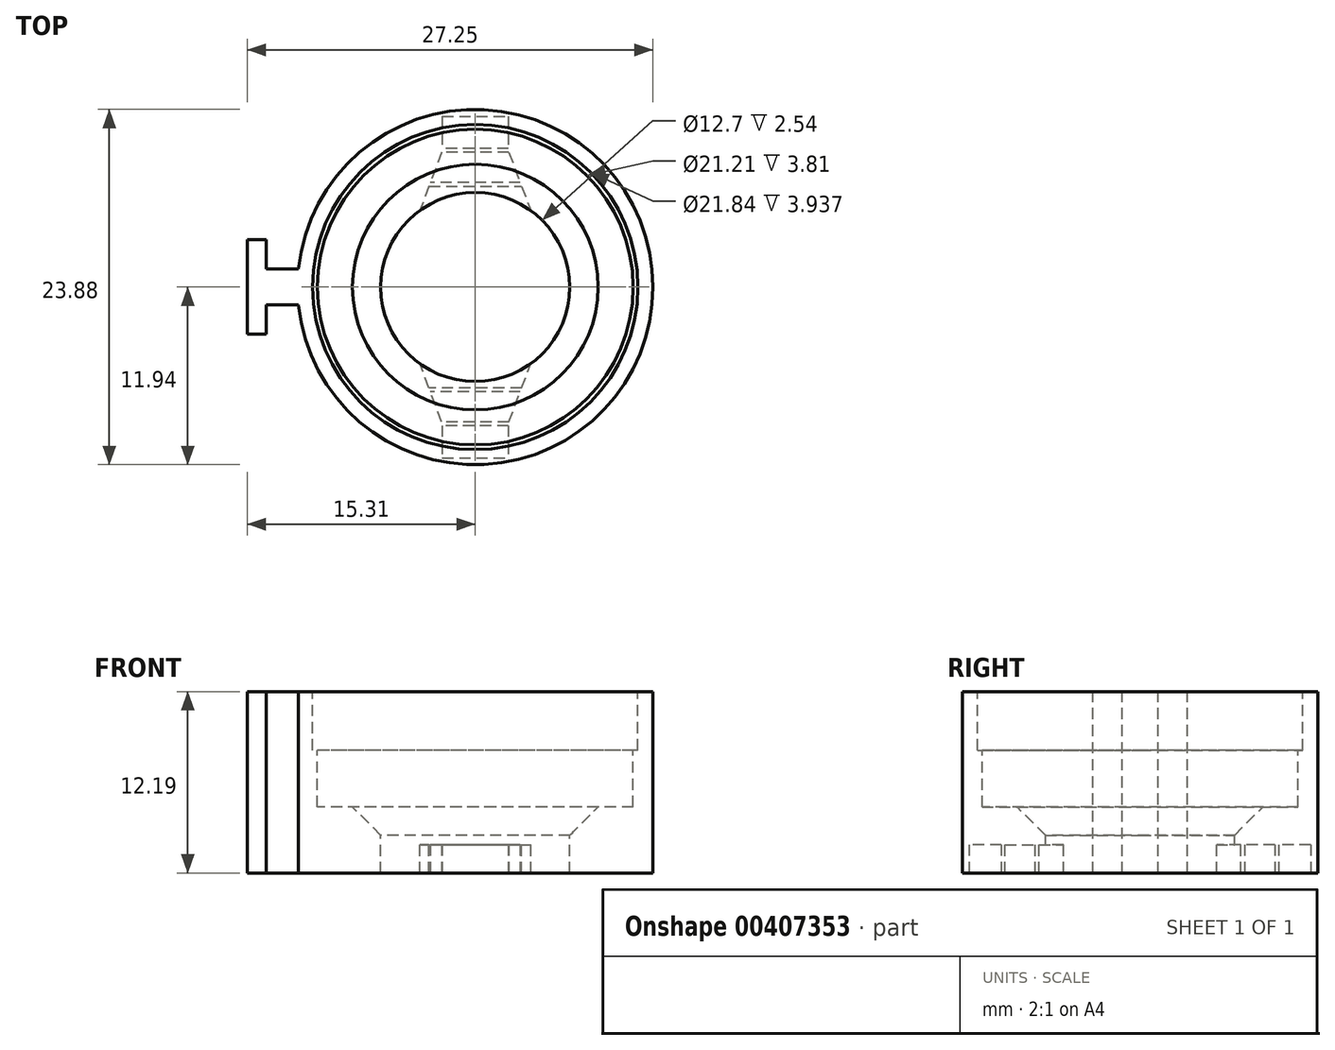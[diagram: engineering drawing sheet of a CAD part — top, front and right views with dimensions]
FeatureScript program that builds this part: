
annotation { "Feature Type Name" : "Feature", "Feature Type Description" : "" }
export const myFeature = defineFeature(function(context is Context, id is Id, definition is map)
    precondition{}
    {
        {
            var Q0;
            Q0=qCreatedBy(makeId("Top.planeOp"),FACE);
            var sketch = newSketch(context, id + "F0", { "sketchPlane" : qUnion([Q0])});
            skCircle(sketch, "E0", {"center": v(0, 0) * mm, "radius": 11.94 * mm});
            skSolve(sketch);
        }
        {
            var Q0;
            Q0 = qSketchRegion(id + "F0", true);
            extrude(context, id + "F1", {"entities" : qUnion([Q0]), "oppositeDirection" : true, "depth" : 12.2 * mm});
        }
        {
            var Q0;
            Q0=makeQuery(id+"F1.opExtrude","CAP_FACE",FACE,{"disambiguationData":[OSD([sQuery(id+"F0.wireOp",EDGE,"E0")])],"isStart":true});
            var sketch = newSketch(context, id + "F2", { "sketchPlane" : qUnion([Q0])});
            skCircle(sketch, "E1", {"center": v(0, 0) * mm, "radius": 6.35 * mm});
            skSolve(sketch);
        }
        {
            var Q0;
            Q0 = qSketchRegion(id + "F2", true);
            extrude(context, id + "F3", {"entities" : qUnion([Q0]), "operationType" : NewBodyOperationType.REMOVE, "endBound" : BoundingType.THROUGH_ALL, "oppositeDirection" : true, "depth" : 25.4 * mm});
        }
        {
            var Q0;
            Q0=makeQuery(id+"F1.opExtrude","CAP_FACE",FACE,{"disambiguationData":[OSD([sQuery(id+"F0.wireOp",EDGE,"E0")])],"isStart":true});
            var sketch = newSketch(context, id + "F4", { "sketchPlane" : qUnion([Q0])});
            skCircle(sketch, "E2", {"center": v(0, 0) * mm, "radius": 10.6 * mm});
            skSolve(sketch);
        }
        {
            var Q0;
            Q0 = qSketchRegion(id + "F4", true);
            extrude(context, id + "F5", {"entities" : qUnion([Q0]), "operationType" : NewBodyOperationType.REMOVE, "oppositeDirection" : true, "depth" : 7.75 * mm});
        }
        {
            var Q0;
            Q0=makeQuery(id+"F5.boolean.opBoolean","INTERSECT",EDGE,{"derivedFrom":[makeQuery(id+"F3.boolean.opBoolean","COPY",FACE,{"derivedFrom":makeQuery(id+"F3.opExtrude","SWEPT_FACE",FACE,{"disambiguationData":[OSD([sQuery(id+"F2.wireOp",EDGE,"E1")])]})}),makeQuery(id+"F5.opExtrude","CAP_FACE",FACE,{"disambiguationData":[OSD([sQuery(id+"F4.wireOp",EDGE,"E2")])],"isStart":false})]});
            chamfer(context, id + "F6", {"entities" : qUnion([Q0]), "width" : 1.9 * mm, "tangentPropagation" : true});
        }
        {
            var Q0;
            Q0=qCreatedBy(makeId("Top.planeOp"),FACE);
            var sketch = newSketch(context, id + "F7", { "sketchPlane" : qUnion([Q0])});
            skCircle(sketch, "E3", {"center": v(0, 0) * mm, "radius": 10.92 * mm});
            skSolve(sketch);
        }
        {
            var Q0;
            Q0 = qSketchRegion(id + "F7", true);
            extrude(context, id + "F8", {"entities" : qUnion([Q0]), "operationType" : NewBodyOperationType.REMOVE, "oppositeDirection" : true, "depth" : 3.94 * mm});
        }
        {
            var Q0;
            Q0=makeQuery(id+"F1.opExtrude","CAP_FACE",FACE,{"disambiguationData":[OSD([sQuery(id+"F0.wireOp",EDGE,"E0")])],"isStart":false});
            var sketch = newSketch(context, id + "F9", { "sketchPlane" : qUnion([Q0])});
            skLineSegment(sketch, "E4.bottom", {"start": v(2.22, -11.94) * mm, "end": v(-2.22, -11.94) * mm});
            skLineSegment(sketch, "E4.top", {"start": v(2.22, 11.94) * mm, "end": v(-2.22, 11.94) * mm});
            skLineSegment(sketch, "E4.left", {"start": v(2.22, -11.94) * mm, "end": v(2.22, 11.94) * mm});
            skLineSegment(sketch, "E4.right", {"start": v(-2.22, -11.94) * mm, "end": v(-2.22, 11.94) * mm});
            skPoint(sketch, "E4.middle", {"position": v(0, 0) * mm});
            skSolve(sketch);
        }
        {
            var Q0;
            Q0 = qSketchRegion(id + "F9", true);
            extrude(context, id + "F10", {"entities" : qUnion([Q0]), "operationType" : NewBodyOperationType.REMOVE, "oppositeDirection" : true, "depth" : 1.9 * mm});
        }
        {
            var Q0;
            {var subQ0=sQuery(id+"F0.wireOp",EDGE,"E0");Q0=makeQuery(id+"F10.boolean.opBoolean","SPLIT",FACE,{"disambiguationData":[TD([makeQuery(id+"F10.opExtrude","SWEPT_FACE",FACE,{"disambiguationData":[OSD([sQuery(id+"F9.wireOp",EDGE,"E4.right")])]})])],"derivedFrom":makeQuery(id+"F1.opExtrude","CAP_FACE",FACE,{"disambiguationData":[OSD([subQ0])],"isStart":false})});}
            cPlane(context, id + "F11", {"entities" : qUnion([Q0]), "cplaneType" : CPlaneType.OFFSET, "offset" : 0 * mm, "width" : 152.4 * mm, "height" : 152.4 * mm});
        }
        {
            var Q0;
            Q0=qCreatedBy(id+"F11.planeOp",FACE);
            var sketch = newSketch(context, id + "F12", { "sketchPlane" : qUnion([Q0])});
            skLineSegment(sketch, "E5", {"start": v(-27.4, 0) * mm, "end": v(27.4, 0) * mm, "construction": true});
            skLineSegment(sketch, "E6", {"start": v(0, 19.3) * mm, "end": v(0, -27.43) * mm, "construction": true});
            skLineSegment(sketch, "E7", {"start": v(-2.22, 9.14) * mm, "end": v(-5.08, 1.52) * mm});
            skLineSegment(sketch, "E8", {"start": v(-5.08, 1.52) * mm, "end": v(0, 1.52) * mm});
            skLineSegment(sketch, "E9", {"start": v(0, 1.52) * mm, "end": v(0, 9.14) * mm});
            skLineSegment(sketch, "E10", {"start": v(-2.22, 9.14) * mm, "end": v(0, 9.14) * mm});
            skLineSegment(sketch, "E11.MirrorCS", {"start": v(5.08, 1.52) * mm, "end": v(0, 1.52) * mm});
            skLineSegment(sketch, "E12.MirrorCS", {"start": v(2.22, 9.14) * mm, "end": v(0, 9.14) * mm});
            skLineSegment(sketch, "E13.MirrorCS", {"start": v(2.22, 9.14) * mm, "end": v(5.08, 1.52) * mm});
            skLineSegment(sketch, "E14.MirrorCS", {"start": v(2.22, -9.14) * mm, "end": v(0, -9.14) * mm});
            skLineSegment(sketch, "E15.MirrorCS", {"start": v(2.22, -9.14) * mm, "end": v(5.08, -1.52) * mm});
            skLineSegment(sketch, "E16.MirrorCS", {"start": v(5.08, -1.52) * mm, "end": v(0, -1.52) * mm});
            skLineSegment(sketch, "E17.MirrorCS", {"start": v(-5.08, -1.52) * mm, "end": v(0, -1.52) * mm});
            skLineSegment(sketch, "E18.MirrorCS", {"start": v(-2.22, -9.14) * mm, "end": v(0, -9.14) * mm});
            skLineSegment(sketch, "E19.MirrorCS", {"start": v(-2.22, -9.14) * mm, "end": v(-5.08, -1.52) * mm});
            skSolve(sketch);
        }
        {
            var Q0;
            Q0 = qSketchRegion(id + "F12", true);
            extrude(context, id + "F13", {"entities" : qUnion([Q0]), "operationType" : NewBodyOperationType.REMOVE, "oppositeDirection" : true, "depth" : 1.9 * mm});
        }
        {
            var Q0;
            Q0=qCreatedBy(id+"F11.planeOp",FACE);
            var sketch = newSketch(context, id + "F14", { "sketchPlane" : qUnion([Q0])});
            skLineSegment(sketch, "E20", {"start": v(-2.22, 11.73) * mm, "end": v(-2.22, 11.48) * mm});
            skLineSegment(sketch, "E21", {"start": v(2.22, 11.48) * mm, "end": v(2.22, 11.73) * mm});
            skLineSegment(sketch, "E22", {"start": v(-2.22, 11.48) * mm, "end": v(2.22, 11.48) * mm});
            skArc(sketch, "E23.0", {"start": v(-2.22, 11.73) * mm, "mid": v(0, 11.94) * mm, "end": v(2.22, 11.73) * mm});
            skLineSegment(sketch, "E24", {"start": v(0, 12.52) * mm, "end": v(0, 4.82) * mm, "construction": true});
            skPoint(sketch, "E24.endSnap0", {"position": v(0, 11.48) * mm});
            skLineSegment(sketch, "E25.bottom", {"start": v(3.3, 9.32) * mm, "end": v(-3.3, 9.32) * mm});
            skLineSegment(sketch, "E25.top", {"start": v(3.3, 9.06) * mm, "end": v(-3.3, 9.06) * mm});
            skLineSegment(sketch, "E25.left", {"start": v(3.3, 9.32) * mm, "end": v(3.3, 9.06) * mm});
            skLineSegment(sketch, "E25.right", {"start": v(-3.3, 9.32) * mm, "end": v(-3.3, 9.06) * mm});
            skPoint(sketch, "E25.middle", {"position": v(0, 9.19) * mm});
            skLineSegment(sketch, "E26.bottom", {"start": v(3.3, 6.78) * mm, "end": v(-3.3, 6.78) * mm});
            skLineSegment(sketch, "E26.top", {"start": v(3.3, 7.03) * mm, "end": v(-3.3, 7.03) * mm});
            skLineSegment(sketch, "E26.left", {"start": v(3.3, 6.78) * mm, "end": v(3.3, 7.03) * mm});
            skLineSegment(sketch, "E26.right", {"start": v(-3.3, 6.78) * mm, "end": v(-3.3, 7.03) * mm});
            skPoint(sketch, "E26.middle", {"position": v(0, 6.9) * mm});
            skLineSegment(sketch, "E27", {"start": v(-21.2, 0) * mm, "end": v(24.32, 0) * mm, "construction": true});
            skLineSegment(sketch, "E28.MirrorCS", {"start": v(-2.22, 11.48) * mm, "end": v(-2.22, 11.73) * mm});
            skLineSegment(sketch, "E29.MirrorCS", {"start": v(2.22, 11.48) * mm, "end": v(-2.22, 11.48) * mm});
            skLineSegment(sketch, "E30.MirrorCS", {"start": v(2.22, 11.73) * mm, "end": v(2.22, 11.48) * mm});
            skLineSegment(sketch, "E31.MirrorCS", {"start": v(-3.3, 9.32) * mm, "end": v(3.3, 9.32) * mm});
            skArc(sketch, "E32.MirrorCS", {"start": v(2.22, 11.73) * mm, "mid": v(0, 11.94) * mm, "end": v(-2.22, 11.73) * mm});
            skLineSegment(sketch, "E33.MirrorCS", {"start": v(-3.3, 9.06) * mm, "end": v(3.3, 9.06) * mm});
            skLineSegment(sketch, "E34.MirrorCS", {"start": v(-3.3, 6.78) * mm, "end": v(3.3, 6.78) * mm});
            skLineSegment(sketch, "E35.MirrorCS", {"start": v(-3.3, 7.03) * mm, "end": v(3.3, 7.03) * mm});
            skLineSegment(sketch, "E36.MirrorCS", {"start": v(21.2, 0) * mm, "end": v(-24.32, 0) * mm, "construction": true});
            skLineSegment(sketch, "E37.MirrorCS", {"start": v(-3.3, -6.78) * mm, "end": v(-3.3, -7.03) * mm});
            skLineSegment(sketch, "E38.MirrorCS", {"start": v(3.3, -6.78) * mm, "end": v(3.3, -7.03) * mm});
            skLineSegment(sketch, "E39.MirrorCS", {"start": v(-3.3, -9.32) * mm, "end": v(-3.3, -9.06) * mm});
            skLineSegment(sketch, "E40.MirrorCS", {"start": v(2.22, -11.73) * mm, "end": v(2.22, -11.48) * mm});
            skLineSegment(sketch, "E41.MirrorCS", {"start": v(3.3, -9.32) * mm, "end": v(3.3, -9.06) * mm});
            skLineSegment(sketch, "E42.MirrorCS", {"start": v(-2.22, -11.48) * mm, "end": v(-2.22, -11.73) * mm});
            skLineSegment(sketch, "E43.MirrorCS", {"start": v(-2.22, -11.73) * mm, "end": v(-2.22, -11.48) * mm});
            skLineSegment(sketch, "E44.MirrorCS", {"start": v(2.22, -11.48) * mm, "end": v(2.22, -11.73) * mm});
            skLineSegment(sketch, "E45.MirrorCS", {"start": v(3.3, -9.06) * mm, "end": v(-3.3, -9.06) * mm});
            skPoint(sketch, "E46.MirrorP", {"position": v(0, -6.9) * mm});
            skPoint(sketch, "E47.MirrorP", {"position": v(0, -9.19) * mm});
            skLineSegment(sketch, "E48.MirrorCS", {"start": v(-2.22, -11.48) * mm, "end": v(2.22, -11.48) * mm});
            skLineSegment(sketch, "E49.MirrorCS", {"start": v(3.3, -7.03) * mm, "end": v(-3.3, -7.03) * mm});
            skLineSegment(sketch, "E50.MirrorCS", {"start": v(3.3, -9.32) * mm, "end": v(-3.3, -9.32) * mm});
            skLineSegment(sketch, "E51.MirrorCS", {"start": v(-3.3, -6.78) * mm, "end": v(3.3, -6.78) * mm});
            skPoint(sketch, "E52.MirrorP", {"position": v(0, -11.48) * mm});
            skArc(sketch, "E53.MirrorCS", {"start": v(-2.22, -11.73) * mm, "mid": v(0, -11.94) * mm, "end": v(2.22, -11.73) * mm});
            skLineSegment(sketch, "E54.MirrorCS", {"start": v(-3.3, -9.32) * mm, "end": v(3.3, -9.32) * mm});
            skLineSegment(sketch, "E55.MirrorCS", {"start": v(-3.3, -7.03) * mm, "end": v(3.3, -7.03) * mm});
            skLineSegment(sketch, "E56.MirrorCS", {"start": v(3.3, -6.78) * mm, "end": v(-3.3, -6.78) * mm});
            skLineSegment(sketch, "E57.MirrorCS", {"start": v(2.22, -11.48) * mm, "end": v(-2.22, -11.48) * mm});
            skLineSegment(sketch, "E58.MirrorCS", {"start": v(-3.3, -9.06) * mm, "end": v(3.3, -9.06) * mm});
            skArc(sketch, "E59.MirrorCS", {"start": v(2.22, -11.73) * mm, "mid": v(0, -11.94) * mm, "end": v(-2.22, -11.73) * mm});
            skSolve(sketch);
        }
        {
            var Q0;
            Q0 = qSketchRegion(id + "F14", true);
            extrude(context, id + "F15", {"entities" : qUnion([Q0]), "operationType" : NewBodyOperationType.ADD, "oppositeDirection" : true, "depth" : 2.54 * mm});
        }
        {
            var Q0;
            Q0=qCreatedBy(makeId("Top.planeOp"),FACE);
            var sketch = newSketch(context, id + "F16", { "sketchPlane" : qUnion([Q0])});
            skLineSegment(sketch, "E60", {"start": v(0.92, 0) * mm, "end": v(-17.34, 0) * mm, "construction": true});
            skLineSegment(sketch, "E61", {"start": v(-11.88, 1.2) * mm, "end": v(-14.04, 1.2) * mm});
            skLineSegment(sketch, "E62", {"start": v(-14.04, 1.2) * mm, "end": v(-14.04, 3.17) * mm});
            skLineSegment(sketch, "E63", {"start": v(-14.04, 3.17) * mm, "end": v(-15.3, 3.17) * mm});
            skLineSegment(sketch, "E64", {"start": v(-15.3, 3.17) * mm, "end": v(-15.3, 0) * mm});
            skLineSegment(sketch, "E65.MirrorCS", {"start": v(-14.04, -1.2) * mm, "end": v(-14.04, -3.17) * mm});
            skLineSegment(sketch, "E66.MirrorCS", {"start": v(-11.88, -1.2) * mm, "end": v(-14.04, -1.2) * mm});
            skLineSegment(sketch, "E67.MirrorCS", {"start": v(-14.04, -3.17) * mm, "end": v(-15.3, -3.17) * mm});
            skLineSegment(sketch, "E68.MirrorCS", {"start": v(-15.3, -3.17) * mm, "end": v(-15.3, 0) * mm});
            skArc(sketch, "E69.0", {"start": v(-11.88, 1.2) * mm, "mid": v(-11.94, 0) * mm, "end": v(-11.88, -1.2) * mm});
            skSolve(sketch);
        }
        {
            var Q0;
            Q0 = qSketchRegion(id + "F16", true);
            extrude(context, id + "F17", {"entities" : qUnion([Q0]), "operationType" : NewBodyOperationType.ADD, "oppositeDirection" : true, "depth" : 12.2 * mm});
        }
    });
